# Revit family: Haworth_Tibas_Desk_DoubleWorkstations_AP_PRELIMINARY1
name_source: partatom
category: Furniture
units: mm (PartAtom-declared; Revit-internal decimal feet)

## family parameters
Always vertical = Yes
Cut with Voids When Loaded = No
OmniClass Number = 23.40.70.14.64.11
OmniClass Title = Office Furniture
Room Calculation Point = No
Shared = No
Work Plane-Based = No

## types (5) — shared parameters
Actual Height = 835 mm
Assembly Code = E2020200
Cable Tray Finish = Haworth _ Paint _ Metallic Silver
Description = Haworth - Tibas - Desk - Double Workstations
Leg Height = 800 mm  [stored 2.62467 ft]
Manufacturer = Haworth
Model = SYTBDWXXXX
Product URL = https://www.haworth.com
Revision Number = 1
Size = Verify Final Dim.w/ Haworth
Trim Finish = Haworth _ Polymer _ Undecided
URL = https://www.haworth.com
Warranty = http://www.haworth.com
With Top = Yes
Worksurface Depth = 1400, 1500, 1600mm
Worksurface Width = 1200, 1400, 1500, 1600, 1800

## per-type parameters (varying)
| type | Accessory Kit | Actual Depth | Actual Width | Cable Tray Double | Cable Tray Single | Cable Tray Width | Flip Top Cable Outlet | Flip Top Width | No Accessory Kit | No Screen | Round Cable Outlet | Top Depth | With Screen |
| 1400w | Yes | 1500 mm  [stored 4.92126 ft] | 1400 mm | No | Yes | 1100 mm | No | 200 mm  [stored 0.656168 ft] | No | Yes | Yes | 1500 mm  [stored 4.92126 ft] | No |
| 1200w | Yes | 1400 mm | 1200 mm | Yes | No | 900 mm  [stored 2.95276 ft] | Yes | 200 mm  [stored 0.656168 ft] | No | No | No | 689 mm | Yes |
| 1500w | No | 1600 mm | 1500 mm  [stored 4.92126 ft] | No | No | 1200 mm | No | 200 mm  [stored 0.656168 ft] | Yes | No | No | 789 mm | Yes |
| 1600w | Yes | 1400 mm | 1600 mm | Yes | No | 1300 mm | Yes | 200 mm  [stored 0.656168 ft] | No | Yes | No | 1400 mm | No |
| 1800w | Yes | 1500 mm  [stored 4.92126 ft] | 1800 mm  [stored 5.90551 ft] | No | Yes | 1500 mm  [stored 4.92126 ft] | No | 400 mm  [stored 1.31234 ft] | No | No | Yes | 739 mm  [stored 2.42454 ft] | Yes |

note: [stored X ft] marks values corroborated as IEEE doubles in the binary element streams (Revit-internal decimal feet)

## geometry (parser evidence)
native form markers: Sweep x25
no freeform markers — native parametric forms only
